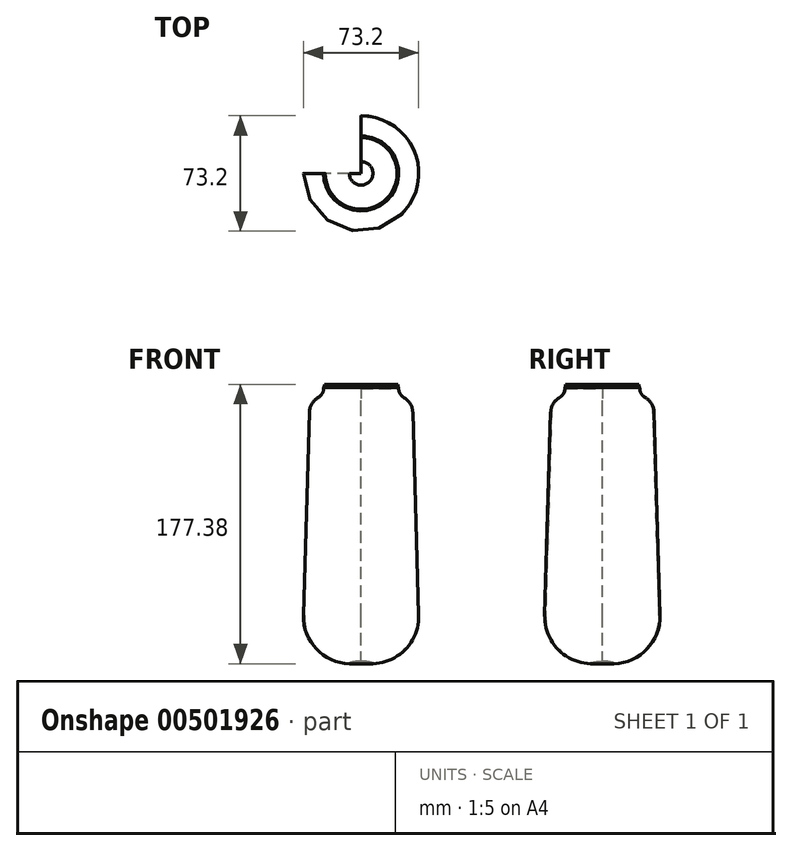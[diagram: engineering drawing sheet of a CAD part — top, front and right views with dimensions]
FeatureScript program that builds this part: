
annotation { "Feature Type Name" : "Feature", "Feature Type Description" : "" }
export const myFeature = defineFeature(function(context is Context, id is Id, definition is map)
    precondition{}
    {
        {
            var Q0;
            Q0=qCreatedBy(makeId("Right.planeOp"),FACE);
            var sketch = newSketch(context, id + "F0", { "sketchPlane" : qUnion([Q0])});
            skLineSegment(sketch, "E0", {"start": v(-36.6, -0.14) * mm, "end": v(-32.8, 128.86) * mm});
            skPoint(sketch, "E1.visualSharp", {"position": v(-37.5, -31.01) * mm});
            skArc(sketch, "E1.filletArc", {"start": v(-36.6, -0.14) * mm, "mid": v(-28.44, -21.6) * mm, "end": v(-7.5, -31.01) * mm});
            skPoint(sketch, "E2.visualSharp", {"position": v(-32.5, 138.91) * mm});
            skArc(sketch, "E2.filletArc", {"start": v(-27.27, 138.08) * mm, "mid": v(-31.23, 134.2) * mm, "end": v(-32.8, 128.86) * mm});
            skPoint(sketch, "E3.visualSharp", {"position": v(-22.18, 128.7) * mm});
            skArc(sketch, "E4", {"start": v(-26.83, 138.36) * mm, "mid": v(-25.47, 139.6) * mm, "end": v(-24.43, 141.12) * mm});
            skPoint(sketch, "E5.visualSharp", {"position": v(-27.11, 138.16) * mm});
            skArc(sketch, "E5.filletArc", {"start": v(-27.27, 138.08) * mm, "mid": v(-27.04, 138.21) * mm, "end": v(-26.83, 138.36) * mm});
            skArc(sketch, "E6", {"start": v(-23.7, 144.4) * mm, "mid": v(-23.83, 144.08) * mm, "end": v(-23.87, 143.72) * mm});
            skPoint(sketch, "E7.visualSharp", {"position": v(-23.7, 143.17) * mm});
            skArc(sketch, "E7.filletArc", {"start": v(-24.43, 141.12) * mm, "mid": v(-23.97, 142.38) * mm, "end": v(-23.87, 143.72) * mm});
            skArc(sketch, "E8", {"start": v(-23.7, 144.4) * mm, "mid": v(-23.4, 145.37) * mm, "end": v(-23.31, 146.37) * mm});
            skArc(sketch, "E9.0", {"start": v(-36.1, -0.16) * mm, "mid": v(-28.07, -21.26) * mm, "end": v(-7.49, -30.51) * mm});
            skLineSegment(sketch, "E9.1", {"start": v(-36.1, -0.16) * mm, "end": v(-32.3, 128.85) * mm});
            skArc(sketch, "E9.2", {"start": v(-27.02, 137.64) * mm, "mid": v(-30.8, 133.93) * mm, "end": v(-32.3, 128.85) * mm});
            skArc(sketch, "E9.3", {"start": v(-23.38, 143.88) * mm, "mid": v(-22.95, 145.1) * mm, "end": v(-22.81, 146.37) * mm});
            skArc(sketch, "E9.4", {"start": v(-23.99, 140.88) * mm, "mid": v(-23.47, 142.34) * mm, "end": v(-23.38, 143.88) * mm});
            skArc(sketch, "E9.5", {"start": v(-26.54, 137.95) * mm, "mid": v(-25.1, 139.27) * mm, "end": v(-23.99, 140.88) * mm});
            skArc(sketch, "E9.6", {"start": v(-27.02, 137.64) * mm, "mid": v(-26.77, 137.8) * mm, "end": v(-26.54, 137.95) * mm});
            skArc(sketch, "E10", {"start": v(0, -29.7) * mm, "mid": v(-3.8, -30.1) * mm, "end": v(-7.5, -31.01) * mm});
            skArc(sketch, "E11", {"start": v(0, -29.45) * mm, "mid": v(-3.78, -29.69) * mm, "end": v(-7.49, -30.51) * mm});
            skLineSegment(sketch, "E12", {"start": v(-23.31, 146.37) * mm, "end": v(-22.81, 146.37) * mm});
            skLineSegment(sketch, "E13", {"start": v(0, -48.85) * mm, "end": v(0, 181.15) * mm});
            skSolve(sketch);
        }
        {
            var Q0;
            Q0 = qSketchRegion(id + "F0", true);
            var Q1;
            Q1=sQuery(id+"F0.wireOp",EDGE,"E13");
            revolve(context, id + "F1", {"entities" : qUnion([Q0]), "axis" : qUnion([Q1]), "revolveType" : RevolveType.FULL});
        }
        {
            var Q0;
            Q0=qCreatedBy(makeId("Right.planeOp"),FACE);
            var sketch = newSketch(context, id + "F2", { "sketchPlane" : qUnion([Q0])});
            skLineSegment(sketch, "E14.bottom", {"start": v(0, -49.42) * mm, "end": v(56.87, -49.42) * mm});
            skLineSegment(sketch, "E14.top", {"start": v(0, 166.7) * mm, "end": v(56.87, 166.7) * mm});
            skLineSegment(sketch, "E14.left", {"start": v(0, -49.42) * mm, "end": v(0, 166.7) * mm});
            skLineSegment(sketch, "E14.right", {"start": v(56.87, -49.42) * mm, "end": v(56.87, 166.7) * mm});
            skSolve(sketch);
        }
        {
            var Q0;
            Q0 = qSketchRegion(id + "F2", true);
            extrude(context, id + "F3", {"entities" : qUnion([Q0]), "operationType" : NewBodyOperationType.REMOVE, "oppositeDirection" : true, "depth" : 58.24 * mm});
        }
    });
